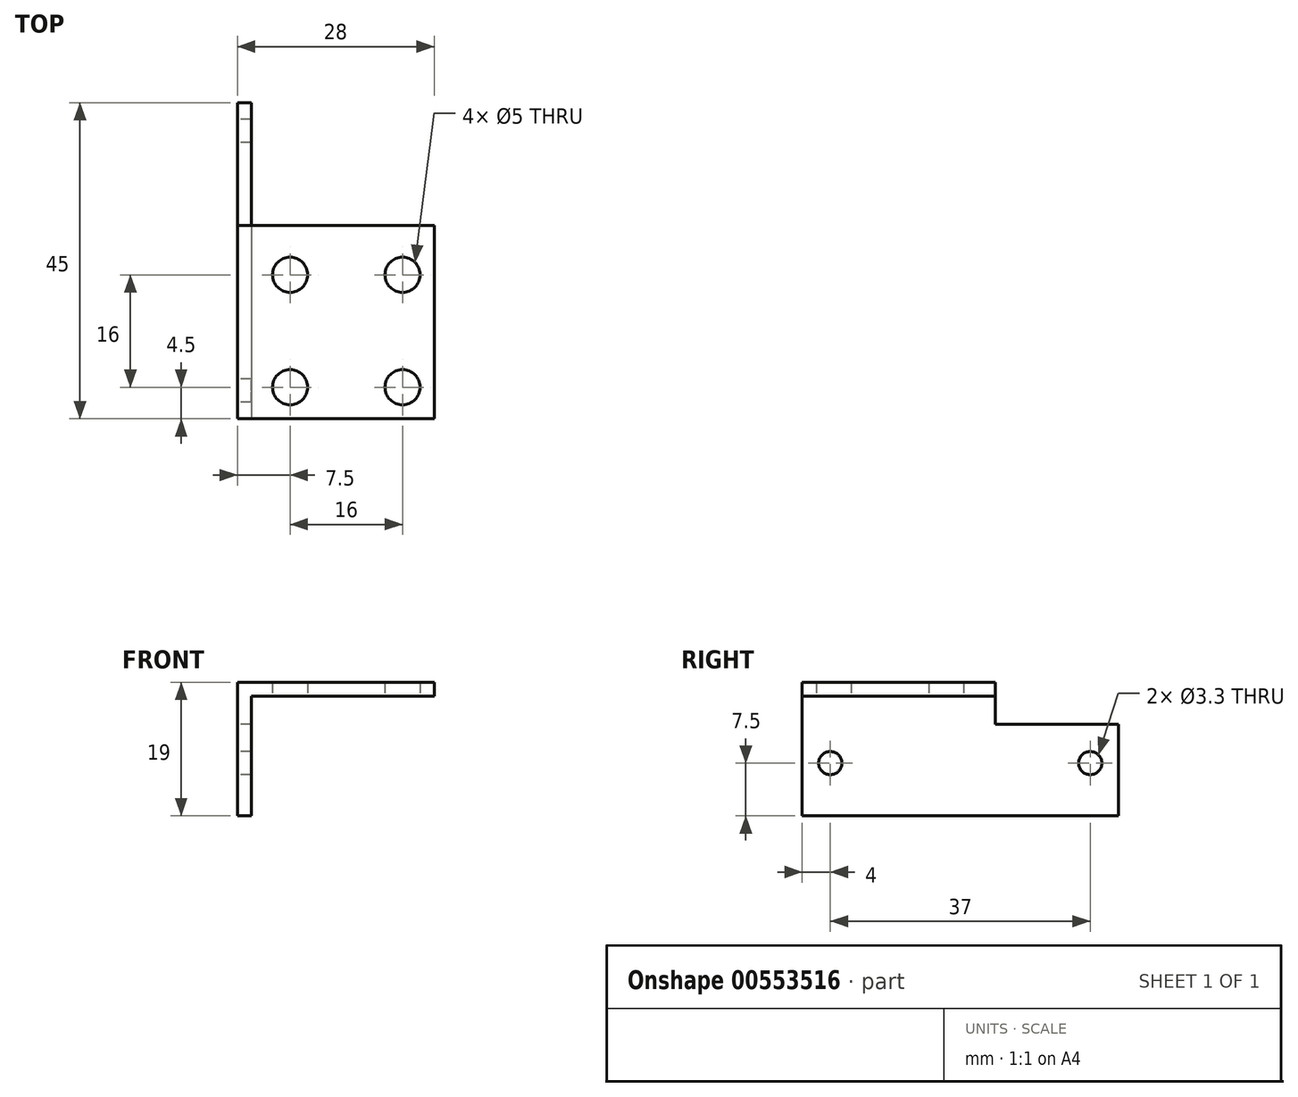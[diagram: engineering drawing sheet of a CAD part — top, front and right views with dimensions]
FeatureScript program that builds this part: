
annotation { "Feature Type Name" : "Feature", "Feature Type Description" : "" }
export const myFeature = defineFeature(function(context is Context, id is Id, definition is map)
    precondition{}
    {
        {
            var Q0;
            Q0=qCreatedBy(makeId("Top.planeOp"),FACE);
            var sketch = newSketch(context, id + "F0", { "sketchPlane" : qUnion([Q0])});
            skLineSegment(sketch, "E0.bottom", {"start": v(-15.5, 22.5) * mm, "end": v(12.5, 22.5) * mm});
            skLineSegment(sketch, "E0.top", {"start": v(-15.5, -22.5) * mm, "end": v(12.5, -22.5) * mm});
            skLineSegment(sketch, "E0.left", {"start": v(-15.5, 22.5) * mm, "end": v(-15.5, -22.5) * mm});
            skLineSegment(sketch, "E0.right", {"start": v(12.5, 22.5) * mm, "end": v(12.5, -22.5) * mm});
            skPoint(sketch, "E1", {"position": v(-8, -18) * mm});
            skPoint(sketch, "E2", {"position": v(8, -18) * mm});
            skPoint(sketch, "E3", {"position": v(8, -2) * mm});
            skPoint(sketch, "E4", {"position": v(-8, -2) * mm});
            skSolve(sketch);
        }
        {
            var Q0;
            Q0=makeQuery(id+"F0.imprint","IMPRINT",FACE,{"disambiguationData":[TD([[makeQuery(id+"F0.imprint","IMPRINT",EDGE,{"derivedFrom":sQuery(id+"F0.wireOp",EDGE,"E0.bottom")}),-1.0]])]});
            extrude(context, id + "F1", {"entities" : qUnion([Q0]), "depth" : 19 * mm, "offsetDistance" : 25 * mm});
        }
        {
            var Q0;
            Q0=sQuery(id+"F0.wireOp",VERTEX,"E3");
            var Q1;
            Q1=sQuery(id+"F0.wireOp",VERTEX,"E4");
            var Q2;
            Q2=sQuery(id+"F0.wireOp",VERTEX,"E1");
            var Q3;
            Q3=sQuery(id+"F0.wireOp",VERTEX,"E2");
            var Q4;
            Q4=makeQuery(id+"F1.opExtrude","SWEPT_BODY",BODY,{"disambiguationData":[OSD([sQuery(id+"F0.wireOp",EDGE,"E0.bottom"),sQuery(id+"F0.wireOp",EDGE,"E0.top"),sQuery(id+"F0.wireOp",EDGE,"E0.left"),sQuery(id+"F0.wireOp",EDGE,"E0.right")])]});
            hole(context, id + "F2", {"style" : HoleStyle.SIMPLE, "endStyle" : HoleEndStyle.THROUGH, "oppositeDirection" : true, "holeDiameter" : 5 * mm, "isTappedThrough" : true, "tappedDepth" : 12 * mm, "tapClearance" : 3, "locations" : qUnion([Q0, Q1, Q2, Q3]), "scope" : qUnion([Q4])});
        }
        {
            var Q0;
            Q0=makeQuery(id+"F1.opExtrude","SWEPT_FACE",FACE,{"disambiguationData":[OSD([sQuery(id+"F0.wireOp",EDGE,"E0.top")])]});
            var sketch = newSketch(context, id + "F3", { "sketchPlane" : qUnion([Q0])});
            skLineSegment(sketch, "E5.bottom", {"start": v(-13.5, 17) * mm, "end": v(12.5, 17) * mm});
            skLineSegment(sketch, "E5.top", {"start": v(-13.5, 0) * mm, "end": v(12.5, 0) * mm});
            skLineSegment(sketch, "E5.left", {"start": v(-13.5, 17) * mm, "end": v(-13.5, 0) * mm});
            skLineSegment(sketch, "E5.right", {"start": v(12.5, 17) * mm, "end": v(12.5, 0) * mm});
            skSolve(sketch);
        }
        {
            var Q0;
            Q0 = qSketchRegion(id + "F3", true);
            extrude(context, id + "F4", {"entities" : qUnion([Q0]), "operationType" : NewBodyOperationType.REMOVE, "endBound" : BoundingType.THROUGH_ALL, "oppositeDirection" : true, "depth" : 25 * mm, "offsetDistance" : 25 * mm});
        }
        {
            var Q0;
            Q0=makeQuery(id+"F1.opExtrude","SWEPT_FACE",FACE,{"disambiguationData":[OSD([sQuery(id+"F0.wireOp",EDGE,"E0.left")])]});
            var sketch = newSketch(context, id + "F5", { "sketchPlane" : qUnion([Q0])});
            skPoint(sketch, "E6", {"position": v(-18.5, 7.5) * mm});
            skPoint(sketch, "E7", {"position": v(18.5, 7.5) * mm});
            skSolve(sketch);
        }
        {
            var Q0;
            Q0=sQuery(id+"F5.wireOp",VERTEX,"E6");
            var Q1;
            Q1=sQuery(id+"F5.wireOp",VERTEX,"E7");
            var Q2;
            Q2=makeQuery(id+"F1.opExtrude","SWEPT_BODY",BODY,{"disambiguationData":[OSD([sQuery(id+"F0.wireOp",EDGE,"E0.bottom"),sQuery(id+"F0.wireOp",EDGE,"E0.top"),sQuery(id+"F0.wireOp",EDGE,"E0.left"),sQuery(id+"F0.wireOp",EDGE,"E0.right")])]});
            hole(context, id + "F6", {"style" : HoleStyle.SIMPLE, "endStyle" : HoleEndStyle.THROUGH, "standardTappedOrClearance" : lookupTablePath({ "standard" : "ISO", "fit" : "Normal", "size" : "M3", "type" : "Clearance" }), "standardBlindInLast" : lookupTablePath({ "fit" : "Standard", "standard" : "ISO", "size" : "M3", "type" : "Clearance" }), "holeDiameter" : 3.3 * mm, "majorDiameter" : 5 * mm, "isTappedThrough" : true, "tappedDepth" : 12 * mm, "tapClearance" : 3, "locations" : qUnion([Q0, Q1]), "scope" : qUnion([Q2])});
        }
        {
            var Q0;
            Q0=makeQuery(id+"F1.opExtrude","SWEPT_FACE",FACE,{"disambiguationData":[OSD([sQuery(id+"F0.wireOp",EDGE,"E0.left")])]});
            var sketch = newSketch(context, id + "F7", { "sketchPlane" : qUnion([Q0])});
            skLineSegment(sketch, "E8.bottom", {"start": v(-22.5, 19) * mm, "end": v(-5, 19) * mm});
            skLineSegment(sketch, "E8.top", {"start": v(-22.5, 13) * mm, "end": v(-5, 13) * mm});
            skLineSegment(sketch, "E8.left", {"start": v(-22.5, 19) * mm, "end": v(-22.5, 13) * mm});
            skLineSegment(sketch, "E8.right", {"start": v(-5, 19) * mm, "end": v(-5, 13) * mm});
            skSolve(sketch);
        }
        {
            var Q0;
            Q0 = qSketchRegion(id + "F7", true);
            extrude(context, id + "F8", {"entities" : qUnion([Q0]), "operationType" : NewBodyOperationType.REMOVE, "endBound" : BoundingType.THROUGH_ALL, "oppositeDirection" : true, "depth" : 25 * mm, "offsetDistance" : 25 * mm});
        }
    });
